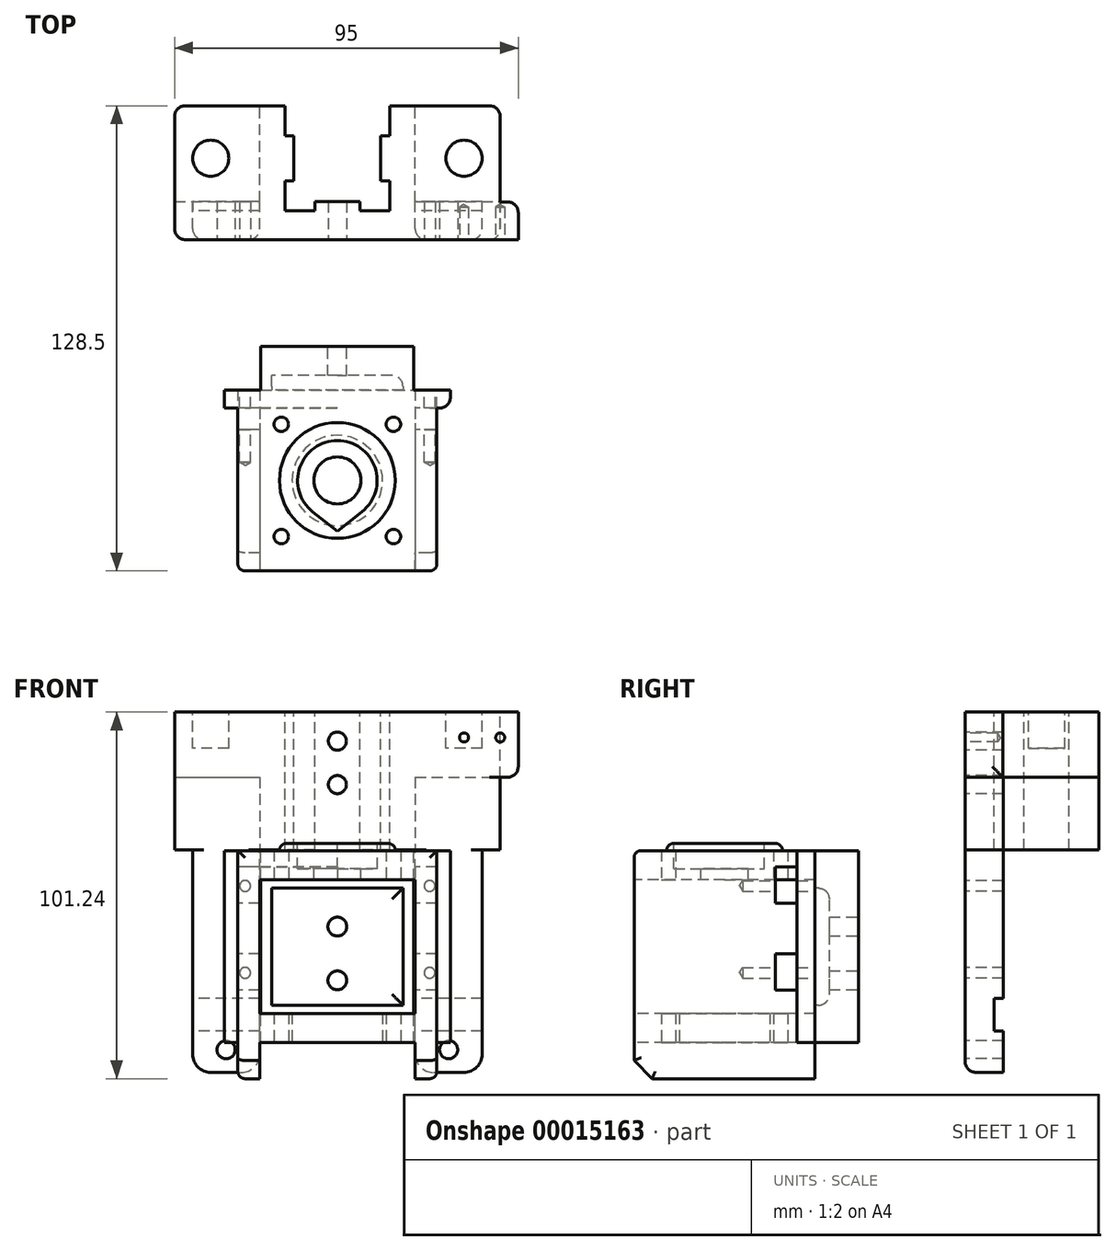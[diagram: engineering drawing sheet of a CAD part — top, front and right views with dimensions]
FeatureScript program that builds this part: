
annotation { "Feature Type Name" : "Feature", "Feature Type Description" : "" }
export const myFeature = defineFeature(function(context is Context, id is Id, definition is map)
    precondition{}
    {
        {
            var Q0;
            Q0=qCreatedBy(makeId("Top.planeOp"),FACE);
            var sketch = newSketch(context, id + "F0", { "sketchPlane" : qUnion([Q0])});
            skLineSegment(sketch, "E0.rect.bottom", {"start": v(-45, -18.5) * mm, "end": v(45, -18.5) * mm});
            skLineSegment(sketch, "E0.rect.top", {"start": v(-45, 18.5) * mm, "end": v(-14.5, 18.5) * mm});
            skLineSegment(sketch, "E0.rect.left", {"start": v(-45, -18.5) * mm, "end": v(-45, 18.5) * mm});
            skLineSegment(sketch, "E0.rect.right", {"start": v(45, -18.5) * mm, "end": v(45, 18.5) * mm});
            skPoint(sketch, "E0.rect.middle", {"position": v(0, 0) * mm});
            skPoint(sketch, "E1", {"position": v(0, 18.5) * mm});
            skLineSegment(sketch, "E2.rect.bottom", {"start": v(14.5, -10.5) * mm, "end": v(6.2, -10.5) * mm});
            skLineSegment(sketch, "E2.rect.left", {"start": v(14.5, -10.5) * mm, "end": v(14.5, -2.2) * mm});
            skLineSegment(sketch, "E2.rect.right", {"start": v(-14.5, -10.5) * mm, "end": v(-14.5, -2.2) * mm});
            skPoint(sketch, "E3.orphan", {"position": v(-14.5, 47.5) * mm});
            skPoint(sketch, "E4.orphan", {"position": v(14.5, 47.5) * mm});
            skLineSegment(sketch, "E5.trimOffspring", {"start": v(14.5, 18.5) * mm, "end": v(45, 18.5) * mm});
            skLineSegment(sketch, "E6", {"start": v(-6.2, -10.5) * mm, "end": v(-6.2, -8) * mm});
            skLineSegment(sketch, "E7", {"start": v(-6.2, -8) * mm, "end": v(6.2, -8) * mm});
            skLineSegment(sketch, "E8", {"start": v(6.2, -8) * mm, "end": v(6.2, -10.5) * mm});
            skLineSegment(sketch, "E9", {"start": v(14.5, 10.2) * mm, "end": v(12, 10.2) * mm});
            skLineSegment(sketch, "E10", {"start": v(12, 10.2) * mm, "end": v(12, -2.2) * mm});
            skLineSegment(sketch, "E11", {"start": v(12, -2.2) * mm, "end": v(14.5, -2.2) * mm});
            skLineSegment(sketch, "E12", {"start": v(-14.5, 10.2) * mm, "end": v(-12, 10.2) * mm});
            skLineSegment(sketch, "E13", {"start": v(-12, 10.2) * mm, "end": v(-12, -2.2) * mm});
            skLineSegment(sketch, "E14", {"start": v(-12, -2.2) * mm, "end": v(-14.5, -2.2) * mm});
            skLineSegment(sketch, "E15.trimOffspring", {"start": v(-14.5, 10.2) * mm, "end": v(-14.5, 18.5) * mm});
            skLineSegment(sketch, "E16.trimOffspring", {"start": v(14.5, 10.2) * mm, "end": v(14.5, 18.5) * mm});
            skLineSegment(sketch, "E17.trimOffspring", {"start": v(-6.2, -10.5) * mm, "end": v(-14.5, -10.5) * mm});
            skPoint(sketch, "E18", {"position": v(-12, 4) * mm});
            skPoint(sketch, "E19", {"position": v(12, 4) * mm});
            skCircle(sketch, "E20", {"center": v(35, 4) * mm, "radius": 5 * mm});
            skCircle(sketch, "E21", {"center": v(-35, 4) * mm, "radius": 5 * mm});
            skPoint(sketch, "E22", {"position": v(0, -8) * mm});
            skSolve(sketch);
        }
        {
            var Q0;
            Q0=makeQuery(id+"F0.imprint","IMPRINT",FACE,{"disambiguationData":[TD([[makeQuery(id+"F0.imprint","IMPRINT",EDGE,{"derivedFrom":sQuery(id+"F0.wireOp",EDGE,"E0.rect.bottom")}),1.0]])]});
            var Q1;
            Q1=makeQuery(id+"F0.imprint","IMPRINT",FACE,{"disambiguationData":[TD([[makeQuery(id+"F0.imprint","IMPRINT",EDGE,{"derivedFrom":sQuery(id+"F0.wireOp",EDGE,"E21")}),1.0]])]});
            var Q2;
            Q2=makeQuery(id+"F0.imprint","IMPRINT",FACE,{"disambiguationData":[TD([[makeQuery(id+"F0.imprint","IMPRINT",EDGE,{"derivedFrom":sQuery(id+"F0.wireOp",EDGE,"E20")}),1.0]])]});
            extrude(context, id + "F1", {"entities" : qUnion([Q0, Q1, Q2]), "oppositeDirection" : true, "depth" : 38 * mm});
        }
        {
            var Q0;
            Q0=makeQuery(id+"F0.imprint","IMPRINT",FACE,{"disambiguationData":[TD([[makeQuery(id+"F0.imprint","IMPRINT",EDGE,{"derivedFrom":sQuery(id+"F0.wireOp",EDGE,"E21")}),1.0]])]});
            var Q1;
            Q1=makeQuery(id+"F0.imprint","IMPRINT",FACE,{"disambiguationData":[TD([[makeQuery(id+"F0.imprint","IMPRINT",EDGE,{"derivedFrom":sQuery(id+"F0.wireOp",EDGE,"E20")}),1.0]])]});
            extrude(context, id + "F2", {"entities" : qUnion([Q0, Q1]), "operationType" : NewBodyOperationType.REMOVE, "oppositeDirection" : true, "depth" : 10 * mm});
        }
        {
            var Q0;
            Q0=makeQuery(id+"F1.opExtrude","CAP_FACE",FACE,{"disambiguationData":[OSD([sQuery(id+"F0.wireOp",EDGE,"E0.rect.bottom"),sQuery(id+"F0.wireOp",EDGE,"E0.rect.top"),sQuery(id+"F0.wireOp",EDGE,"E0.rect.left"),sQuery(id+"F0.wireOp",EDGE,"E0.rect.right"),sQuery(id+"F0.wireOp",EDGE,"E2.rect.bottom"),sQuery(id+"F0.wireOp",EDGE,"E2.rect.left"),sQuery(id+"F0.wireOp",EDGE,"E2.rect.right"),sQuery(id+"F0.wireOp",EDGE,"E5.trimOffspring"),sQuery(id+"F0.wireOp",EDGE,"E6"),sQuery(id+"F0.wireOp",EDGE,"E7"),sQuery(id+"F0.wireOp",EDGE,"E8"),sQuery(id+"F0.wireOp",EDGE,"E9"),sQuery(id+"F0.wireOp",EDGE,"E10"),sQuery(id+"F0.wireOp",EDGE,"E11"),sQuery(id+"F0.wireOp",EDGE,"E12"),sQuery(id+"F0.wireOp",EDGE,"E13"),sQuery(id+"F0.wireOp",EDGE,"E14"),sQuery(id+"F0.wireOp",EDGE,"E15.trimOffspring"),sQuery(id+"F0.wireOp",EDGE,"E16.trimOffspring"),sQuery(id+"F0.wireOp",EDGE,"E17.trimOffspring")])],"isStart":false});
            var sketch = newSketch(context, id + "F3", { "sketchPlane" : qUnion([Q0])});
            skLineSegment(sketch, "E23.0", {"start": v(-6.2, 10.5) * mm, "end": v(-14.5, 10.5) * mm});
            skPoint(sketch, "E23.1", {"position": v(-14.5, 10.5) * mm});
            skLineSegment(sketch, "E23.2", {"start": v(14.5, 10.5) * mm, "end": v(6.2, 10.5) * mm});
            skLineSegment(sketch, "E23.3", {"start": v(-45, 18.5) * mm, "end": v(45, 18.5) * mm});
            skLineSegment(sketch, "E23.4", {"start": v(14.5, 10.5) * mm, "end": v(14.5, 2.2) * mm});
            skLineSegment(sketch, "E23.5", {"start": v(12, 2.2) * mm, "end": v(14.5, 2.2) * mm});
            skLineSegment(sketch, "E23.6", {"start": v(12, -10.2) * mm, "end": v(12, 2.2) * mm});
            skLineSegment(sketch, "E23.7", {"start": v(14.5, -10.2) * mm, "end": v(12, -10.2) * mm});
            skLineSegment(sketch, "E23.8", {"start": v(14.5, -10.2) * mm, "end": v(14.5, -18.5) * mm});
            skLineSegment(sketch, "E23.9", {"start": v(6.2, 8) * mm, "end": v(6.2, 10.5) * mm});
            skLineSegment(sketch, "E23.10", {"start": v(-6.2, 8) * mm, "end": v(6.2, 8) * mm});
            skLineSegment(sketch, "E23.11", {"start": v(-6.2, 10.5) * mm, "end": v(-6.2, 8) * mm});
            skLineSegment(sketch, "E23.12", {"start": v(-14.5, 10.5) * mm, "end": v(-14.5, 2.2) * mm});
            skLineSegment(sketch, "E23.13", {"start": v(-12, 2.2) * mm, "end": v(-14.5, 2.2) * mm});
            skLineSegment(sketch, "E23.14", {"start": v(-12, -10.2) * mm, "end": v(-12, 2.2) * mm});
            skLineSegment(sketch, "E23.15", {"start": v(-14.5, -10.2) * mm, "end": v(-12, -10.2) * mm});
            skLineSegment(sketch, "E23.16", {"start": v(-14.5, -10.2) * mm, "end": v(-14.5, -18.5) * mm});
            skLineSegment(sketch, "E23.17", {"start": v(45, 18.5) * mm, "end": v(45, -18.5) * mm});
            skLineSegment(sketch, "E23.18", {"start": v(14.5, -18.5) * mm, "end": v(45, -18.5) * mm});
            skLineSegment(sketch, "E23.19", {"start": v(-45, -18.5) * mm, "end": v(-14.5, -18.5) * mm});
            skLineSegment(sketch, "E23.20", {"start": v(-45, 18.5) * mm, "end": v(-45, -18.5) * mm});
            skPoint(sketch, "E24", {"position": v(0, 18.5) * mm});
            skLineSegment(sketch, "E25", {"start": v(-21.5, 18.5) * mm, "end": v(-21.5, -18.5) * mm});
            skLineSegment(sketch, "E26", {"start": v(21.5, 18.5) * mm, "end": v(21.5, -18.5) * mm});
            skLineSegment(sketch, "E27", {"start": v(-45, 8) * mm, "end": v(-21.5, 8) * mm});
            skLineSegment(sketch, "E28", {"start": v(21.5, 8) * mm, "end": v(45, 8) * mm});
            skLineSegment(sketch, "E29", {"start": v(40, 18.5) * mm, "end": v(40, 8) * mm});
            skLineSegment(sketch, "E30", {"start": v(-40, 18.5) * mm, "end": v(-40, 8) * mm});
            skSolve(sketch);
        }
        {
            var Q0;
            {var subQ4=sQuery(id+"F3.wireOp",EDGE,"E23.19");var subQ6=sQuery(id+"F3.wireOp",EDGE,"E23.20");var subQ8=makeQuery(id+"F3.imprint","INTERSECT",VERTEX,{"derivedFrom":[subQ4,subQ6]});Q0=makeQuery(id+"F3.imprint","IMPRINT",FACE,{"disambiguationData":[TD([[makeQuery(id+"F3.imprint","IMPRINT",EDGE,{"disambiguationData":[TD([[subQ8,-1.0]])],"derivedFrom":subQ4}),1.0]])]});}
            var Q1;
            {var subQ4=sQuery(id+"F3.wireOp",EDGE,"E23.17");var subQ6=sQuery(id+"F3.wireOp",EDGE,"E23.18");var subQ8=makeQuery(id+"F3.imprint","INTERSECT",VERTEX,{"derivedFrom":[subQ4,subQ6]});Q1=makeQuery(id+"F3.imprint","IMPRINT",FACE,{"disambiguationData":[TD([[makeQuery(id+"F3.imprint","IMPRINT",EDGE,{"disambiguationData":[TD([[subQ8,1.0]])],"derivedFrom":subQ4}),-1.0]])]});}
            extrude(context, id + "F4", {"entities" : qUnion([Q0, Q1]), "operationType" : NewBodyOperationType.REMOVE, "oppositeDirection" : true, "depth" : 20 * mm});
        }
        {
            var Q0;
            {var subQ0=sQuery(id+"F3.wireOp",EDGE,"E30");Q0=makeQuery(id+"F3.imprint","IMPRINT",FACE,{"disambiguationData":[TD([[makeQuery(id+"F3.imprint","IMPRINT",EDGE,{"derivedFrom":subQ0}),1.0]])]});}
            var Q1;
            {var subQ0=sQuery(id+"F3.wireOp",EDGE,"E29");Q1=makeQuery(id+"F3.imprint","IMPRINT",FACE,{"disambiguationData":[TD([[makeQuery(id+"F3.imprint","IMPRINT",EDGE,{"derivedFrom":subQ0}),-1.0]])]});}
            extrude(context, id + "F5", {"entities" : qUnion([Q0, Q1]), "operationType" : NewBodyOperationType.ADD, "depth" : 61.5 * mm});
        }
        {
            var Q0;
            Q0=makeQuery(id+"F5.opExtrude","SWEPT_FACE",FACE,{"disambiguationData":[OSD([sQuery(id+"F3.wireOp",EDGE,"E30")])]});
            var sketch = newSketch(context, id + "F6", { "sketchPlane" : qUnion([Q0])});
            skLineSegment(sketch, "E31.0", {"start": v(18.5, -38) * mm, "end": v(-18.5, -38) * mm});
            skLineSegment(sketch, "E32.bottom", {"start": v(8, -79.1) * mm, "end": v(10.5, -79.1) * mm});
            skLineSegment(sketch, "E32.top", {"start": v(8, -88.1) * mm, "end": v(10.5, -88.1) * mm});
            skLineSegment(sketch, "E32.left", {"start": v(8, -79.1) * mm, "end": v(8, -88.1) * mm});
            skLineSegment(sketch, "E32.right", {"start": v(10.5, -79.1) * mm, "end": v(10.5, -88.1) * mm});
            skSolve(sketch);
        }
        {
            var Q0;
            Q0=makeQuery(id+"F6.imprint","IMPRINT",FACE,{"disambiguationData":[TD([[makeQuery(id+"F6.imprint","IMPRINT",EDGE,{"derivedFrom":sQuery(id+"F6.wireOp",EDGE,"E32.bottom")}),-1.0]])]});
            extrude(context, id + "F7", {"entities" : qUnion([Q0]), "operationType" : NewBodyOperationType.REMOVE, "endBound" : BoundingType.THROUGH_ALL, "oppositeDirection" : true, "depth" : 25 * mm});
        }
        {
            var Q0;
            {var subQ0=sQuery(id+"F3.wireOp",EDGE,"E23.3");Q0=makeQuery(id+"F5.boolean.opBoolean","MERGE",FACE,{"derivedFrom":[makeQuery(id+"F1.opExtrude","SWEPT_FACE",FACE,{"disambiguationData":[OSD([sQuery(id+"F0.wireOp",EDGE,"E0.rect.bottom")])]}),makeQuery(id+"F5.opExtrude","SWEPT_FACE",FACE,{"disambiguationData":[OSD([subQ0]),TDD([makeQuery(id+"F3.imprint","IMPRINT",EDGE,{"disambiguationData":[TD([[makeQuery(id+"F3.imprint","INTERSECT",VERTEX,{"derivedFrom":[subQ0,sQuery(id+"F3.wireOp",EDGE,"E25")]}),1.0]])],"derivedFrom":subQ0})])]}),makeQuery(id+"F5.opExtrude","SWEPT_FACE",FACE,{"disambiguationData":[OSD([subQ0]),TDD([makeQuery(id+"F3.imprint","IMPRINT",EDGE,{"disambiguationData":[TD([[makeQuery(id+"F3.imprint","INTERSECT",VERTEX,{"derivedFrom":[subQ0,sQuery(id+"F3.wireOp",EDGE,"E26")]}),-1.0]])],"derivedFrom":subQ0})])]})]});}
            var sketch = newSketch(context, id + "F8", { "sketchPlane" : qUnion([Q0])});
            skPoint(sketch, "E33.0", {"position": v(0, 0) * mm});
            skLineSegment(sketch, "E34.bottom", {"start": v(30, 0) * mm, "end": v(50, 0) * mm});
            skLineSegment(sketch, "E34.right", {"start": v(50, 0) * mm, "end": v(50, -10) * mm});
            skPoint(sketch, "E35", {"position": v(35, -7) * mm});
            skPoint(sketch, "E36", {"position": v(45, -7) * mm});
            skPoint(sketch, "E37", {"position": v(0, -8) * mm});
            skPoint(sketch, "E38", {"position": v(0, -20) * mm});
            skPoint(sketch, "E39", {"position": v(-30.75, -93.25) * mm});
            skPoint(sketch, "E40", {"position": v(30.75, -93.25) * mm});
            skLineSegment(sketch, "E41.0", {"start": v(45, -38) * mm, "end": v(45, -18) * mm});
            skLineSegment(sketch, "E42.0", {"start": v(21.5, -18) * mm, "end": v(45, -18) * mm});
            skPoint(sketch, "E43", {"position": v(-25.5, -48) * mm});
            skPoint(sketch, "E44", {"position": v(-25.5, -72) * mm});
            skPoint(sketch, "E45", {"position": v(25.5, -48) * mm});
            skPoint(sketch, "E46", {"position": v(25.5, -72) * mm});
            skLineSegment(sketch, "E47.0", {"start": v(-40, -99.5) * mm, "end": v(-40, -38) * mm});
            skLineSegment(sketch, "E47.1", {"start": v(40, -99.5) * mm, "end": v(40, -38) * mm});
            skLineSegment(sketch, "E48", {"start": v(-25.5, -48) * mm, "end": v(-40, -48) * mm});
            skLineSegment(sketch, "E49", {"start": v(25.5, -48) * mm, "end": v(40, -48) * mm});
            skLineSegment(sketch, "E50", {"start": v(-25.5, -72) * mm, "end": v(-40, -72) * mm});
            skLineSegment(sketch, "E51", {"start": v(25.5, -72) * mm, "end": v(40, -72) * mm});
            skLineSegment(sketch, "E52.0", {"start": v(40, -88.1) * mm, "end": v(21.5, -88.1) * mm});
            skLineSegment(sketch, "E52.1", {"start": v(-21.5, -88.1) * mm, "end": v(-40, -88.1) * mm});
            skPoint(sketch, "E53", {"position": v(-30.75, -99.5) * mm});
            skLineSegment(sketch, "E54", {"start": v(-30.75, -93.25) * mm, "end": v(-21.5, -93.25) * mm});
            skLineSegment(sketch, "E55", {"start": v(-30.75, -93.25) * mm, "end": v(-40, -93.25) * mm});
            skLineSegment(sketch, "E56", {"start": v(30.75, -93.25) * mm, "end": v(40, -93.25) * mm});
            skLineSegment(sketch, "E57", {"start": v(30.75, -93.25) * mm, "end": v(21.5, -93.25) * mm});
            skLineSegment(sketch, "E58", {"start": v(50, -10) * mm, "end": v(50, -18) * mm});
            skLineSegment(sketch, "E59", {"start": v(50, -18) * mm, "end": v(45, -18) * mm});
            skPoint(sketch, "E60.trimOffspring.end.orphan", {"position": v(45, 0) * mm});
            skSolve(sketch);
        }
        {
            var Q0;
            {var subQ4=sQuery(id+"F8.wireOp",EDGE,"E34.right");Q0=makeQuery(id+"F8.imprint","IMPRINT",FACE,{"disambiguationData":[TD([[makeQuery(id+"F8.imprint","IMPRINT",EDGE,{"derivedFrom":subQ4}),-1.0]])]});}
            extrude(context, id + "F9", {"entities" : qUnion([Q0]), "operationType" : NewBodyOperationType.ADD, "oppositeDirection" : true, "depth" : 10.45 * mm});
        }
        {
            var Q0;
            Q0=sQuery(id+"F8.wireOp",VERTEX,"E36");
            var Q1;
            Q1=sQuery(id+"F8.wireOp",VERTEX,"E35");
            var Q2;
            Q2=makeQuery(id+"F1.opExtrude","SWEPT_BODY",BODY,{"disambiguationData":[OSD([sQuery(id+"F0.wireOp",EDGE,"E0.rect.bottom"),sQuery(id+"F0.wireOp",EDGE,"E0.rect.top"),sQuery(id+"F0.wireOp",EDGE,"E0.rect.left"),sQuery(id+"F0.wireOp",EDGE,"E0.rect.right"),sQuery(id+"F0.wireOp",EDGE,"E2.rect.bottom"),sQuery(id+"F0.wireOp",EDGE,"E2.rect.left"),sQuery(id+"F0.wireOp",EDGE,"E2.rect.right"),sQuery(id+"F0.wireOp",EDGE,"E5.trimOffspring"),sQuery(id+"F0.wireOp",EDGE,"E6"),sQuery(id+"F0.wireOp",EDGE,"E7"),sQuery(id+"F0.wireOp",EDGE,"E8"),sQuery(id+"F0.wireOp",EDGE,"E9"),sQuery(id+"F0.wireOp",EDGE,"E10"),sQuery(id+"F0.wireOp",EDGE,"E11"),sQuery(id+"F0.wireOp",EDGE,"E12"),sQuery(id+"F0.wireOp",EDGE,"E13"),sQuery(id+"F0.wireOp",EDGE,"E14"),sQuery(id+"F0.wireOp",EDGE,"E15.trimOffspring"),sQuery(id+"F0.wireOp",EDGE,"E16.trimOffspring"),sQuery(id+"F0.wireOp",EDGE,"E17.trimOffspring")])]});
            hole(context, id + "F10", {"style" : HoleStyle.SIMPLE, "holeDiameter" : 2.5 * mm, "endStyle" : HoleEndStyle.BLIND, "holeDepth" : 9 * mm, "locations" : qUnion([Q0, Q1]), "scope" : qUnion([Q2])});
        }
        {
            var Q0;
            Q0=sQuery(id+"F8.wireOp",VERTEX,"E38");
            var Q1;
            Q1=sQuery(id+"F8.wireOp",VERTEX,"E37");
            var Q2;
            Q2=makeQuery(id+"F1.opExtrude","SWEPT_BODY",BODY,{"disambiguationData":[OSD([sQuery(id+"F0.wireOp",EDGE,"E0.rect.bottom"),sQuery(id+"F0.wireOp",EDGE,"E0.rect.top"),sQuery(id+"F0.wireOp",EDGE,"E0.rect.left"),sQuery(id+"F0.wireOp",EDGE,"E0.rect.right"),sQuery(id+"F0.wireOp",EDGE,"E2.rect.bottom"),sQuery(id+"F0.wireOp",EDGE,"E2.rect.left"),sQuery(id+"F0.wireOp",EDGE,"E2.rect.right"),sQuery(id+"F0.wireOp",EDGE,"E5.trimOffspring"),sQuery(id+"F0.wireOp",EDGE,"E6"),sQuery(id+"F0.wireOp",EDGE,"E7"),sQuery(id+"F0.wireOp",EDGE,"E8"),sQuery(id+"F0.wireOp",EDGE,"E9"),sQuery(id+"F0.wireOp",EDGE,"E10"),sQuery(id+"F0.wireOp",EDGE,"E11"),sQuery(id+"F0.wireOp",EDGE,"E12"),sQuery(id+"F0.wireOp",EDGE,"E13"),sQuery(id+"F0.wireOp",EDGE,"E14"),sQuery(id+"F0.wireOp",EDGE,"E15.trimOffspring"),sQuery(id+"F0.wireOp",EDGE,"E16.trimOffspring"),sQuery(id+"F0.wireOp",EDGE,"E17.trimOffspring")])]});
            hole(context, id + "F11", {"style" : HoleStyle.SIMPLE, "holeDiameter" : 5 * mm, "endStyle" : HoleEndStyle.THROUGH, "locations" : qUnion([Q0, Q1]), "scope" : qUnion([Q2])});
        }
        {
            var Q0;
            Q0=sQuery(id+"F8.wireOp",VERTEX,"E40");
            var Q1;
            Q1=sQuery(id+"F8.wireOp",VERTEX,"E39");
            var Q2;
            Q2=makeQuery(id+"F1.opExtrude","SWEPT_BODY",BODY,{"disambiguationData":[OSD([sQuery(id+"F0.wireOp",EDGE,"E0.rect.bottom"),sQuery(id+"F0.wireOp",EDGE,"E0.rect.top"),sQuery(id+"F0.wireOp",EDGE,"E0.rect.left"),sQuery(id+"F0.wireOp",EDGE,"E0.rect.right"),sQuery(id+"F0.wireOp",EDGE,"E2.rect.bottom"),sQuery(id+"F0.wireOp",EDGE,"E2.rect.left"),sQuery(id+"F0.wireOp",EDGE,"E2.rect.right"),sQuery(id+"F0.wireOp",EDGE,"E5.trimOffspring"),sQuery(id+"F0.wireOp",EDGE,"E6"),sQuery(id+"F0.wireOp",EDGE,"E7"),sQuery(id+"F0.wireOp",EDGE,"E8"),sQuery(id+"F0.wireOp",EDGE,"E9"),sQuery(id+"F0.wireOp",EDGE,"E10"),sQuery(id+"F0.wireOp",EDGE,"E11"),sQuery(id+"F0.wireOp",EDGE,"E12"),sQuery(id+"F0.wireOp",EDGE,"E13"),sQuery(id+"F0.wireOp",EDGE,"E14"),sQuery(id+"F0.wireOp",EDGE,"E15.trimOffspring"),sQuery(id+"F0.wireOp",EDGE,"E16.trimOffspring"),sQuery(id+"F0.wireOp",EDGE,"E17.trimOffspring")])]});
            hole(context, id + "F12", {"style" : HoleStyle.SIMPLE, "holeDiameter" : 5 * mm, "endStyle" : HoleEndStyle.THROUGH, "locations" : qUnion([Q0, Q1]), "scope" : qUnion([Q2])});
        }
        {
            var Q0;
            Q0=sQuery(id+"F8.wireOp",VERTEX,"E44");
            var Q1;
            Q1=sQuery(id+"F8.wireOp",VERTEX,"E43");
            var Q2;
            Q2=sQuery(id+"F8.wireOp",VERTEX,"E49.start");
            var Q3;
            Q3=sQuery(id+"F8.wireOp",VERTEX,"E46");
            var Q4;
            Q4=makeQuery(id+"F1.opExtrude","SWEPT_BODY",BODY,{"disambiguationData":[OSD([sQuery(id+"F0.wireOp",EDGE,"E0.rect.bottom"),sQuery(id+"F0.wireOp",EDGE,"E0.rect.top"),sQuery(id+"F0.wireOp",EDGE,"E0.rect.left"),sQuery(id+"F0.wireOp",EDGE,"E0.rect.right"),sQuery(id+"F0.wireOp",EDGE,"E2.rect.bottom"),sQuery(id+"F0.wireOp",EDGE,"E2.rect.left"),sQuery(id+"F0.wireOp",EDGE,"E2.rect.right"),sQuery(id+"F0.wireOp",EDGE,"E5.trimOffspring"),sQuery(id+"F0.wireOp",EDGE,"E6"),sQuery(id+"F0.wireOp",EDGE,"E7"),sQuery(id+"F0.wireOp",EDGE,"E8"),sQuery(id+"F0.wireOp",EDGE,"E9"),sQuery(id+"F0.wireOp",EDGE,"E10"),sQuery(id+"F0.wireOp",EDGE,"E11"),sQuery(id+"F0.wireOp",EDGE,"E12"),sQuery(id+"F0.wireOp",EDGE,"E13"),sQuery(id+"F0.wireOp",EDGE,"E14"),sQuery(id+"F0.wireOp",EDGE,"E15.trimOffspring"),sQuery(id+"F0.wireOp",EDGE,"E16.trimOffspring"),sQuery(id+"F0.wireOp",EDGE,"E17.trimOffspring")])]});
            hole(context, id + "F13", {"style" : HoleStyle.SIMPLE, "holeDiameter" : 3 * mm, "endStyle" : HoleEndStyle.THROUGH, "locations" : qUnion([Q0, Q1, Q2, Q3]), "scope" : qUnion([Q4])});
        }
        {
            var Q0;
            Q0=makeQuery(id+"F5.opExtrude","CAP_EDGE",EDGE,{"disambiguationData":[OSD([sQuery(id+"F3.wireOp",EDGE,"E30")])],"isStart":false});
            var Q1;
            Q1=makeQuery(id+"F5.opExtrude","CAP_EDGE",EDGE,{"disambiguationData":[OSD([sQuery(id+"F3.wireOp",EDGE,"E25")])],"isStart":false});
            var Q2;
            Q2=makeQuery(id+"F5.opExtrude","CAP_EDGE",EDGE,{"disambiguationData":[OSD([sQuery(id+"F3.wireOp",EDGE,"E26")])],"isStart":false});
            var Q3;
            Q3=makeQuery(id+"F5.opExtrude","CAP_EDGE",EDGE,{"disambiguationData":[OSD([sQuery(id+"F3.wireOp",EDGE,"E29")])],"isStart":false});
            fillet(context, id + "F14", {"entities" : qUnion([Q0, Q1, Q2, Q3]), "radius" : 5 * mm, "tangentPropagation" : true, "allowEdgeOverflow" : false});
        }
        {
            var Q0;
            Q0=makeQuery(id+"F5.opExtrude","SWEPT_EDGE",EDGE,{"disambiguationData":[OSD([sQuery(id+"F3.wireOp",EDGE,"E23.3"),sQuery(id+"F3.wireOp",EDGE,"E30")])]});
            var Q1;
            Q1=makeQuery(id+"F5.opExtrude","SWEPT_EDGE",EDGE,{"disambiguationData":[OSD([sQuery(id+"F3.wireOp",EDGE,"E23.3"),sQuery(id+"F3.wireOp",EDGE,"E26")])]});
            var Q2;
            Q2=makeQuery(id+"F1.opExtrude","SWEPT_EDGE",EDGE,{"disambiguationData":[OSD([sQuery(id+"F0.wireOp",EDGE,"E0.rect.bottom"),sQuery(id+"F0.wireOp",EDGE,"E0.rect.left")])]});
            var Q3;
            Q3=makeQuery(id+"F1.opExtrude","SWEPT_EDGE",EDGE,{"disambiguationData":[OSD([sQuery(id+"F0.wireOp",EDGE,"E0.rect.bottom"),sQuery(id+"F0.wireOp",EDGE,"E0.rect.right")])]});
            var Q4;
            Q4=makeQuery(id+"F1.opExtrude","SWEPT_EDGE",EDGE,{"disambiguationData":[OSD([sQuery(id+"F0.wireOp",EDGE,"E0.rect.top"),sQuery(id+"F0.wireOp",EDGE,"E0.rect.left")])]});
            var Q5;
            Q5=makeQuery(id+"F1.opExtrude","SWEPT_EDGE",EDGE,{"disambiguationData":[OSD([sQuery(id+"F0.wireOp",EDGE,"E0.rect.right"),sQuery(id+"F0.wireOp",EDGE,"E5.trimOffspring")])]});
            var Q6;
            Q6=makeQuery(id+"F9.opExtrude","CAP_EDGE",EDGE,{"disambiguationData":[OSD([sQuery(id+"F8.wireOp",EDGE,"E34.right"),sQuery(id+"F8.wireOp",EDGE,"E58")])],"isStart":false});
            var Q7;
            Q7=makeQuery(id+"F9.opExtrude","SWEPT_EDGE",EDGE,{"disambiguationData":[OSD([sQuery(id+"F8.wireOp",EDGE,"E58"),sQuery(id+"F8.wireOp",EDGE,"E59")])]});
            var Q8;
            Q8=makeQuery(id+"F4.boolean.opBoolean","COPY",EDGE,{"derivedFrom":makeQuery(id+"F4.opExtrude","SWEPT_EDGE",EDGE,{"disambiguationData":[OSD([sQuery(id+"F3.wireOp",EDGE,"E23.17"),sQuery(id+"F3.wireOp",EDGE,"E28")])]})});
            var Q9;
            Q9=makeQuery(id+"F4.boolean.opBoolean","COPY",EDGE,{"derivedFrom":makeQuery(id+"F4.opExtrude","SWEPT_EDGE",EDGE,{"disambiguationData":[OSD([sQuery(id+"F3.wireOp",EDGE,"E23.20"),sQuery(id+"F3.wireOp",EDGE,"E27")])]})});
            fillet(context, id + "F15", {"entities" : qUnion([Q0, Q1, Q2, Q3, Q4, Q5, Q6, Q7, Q8, Q9]), "radius" : 3 * mm, "tangentPropagation" : true, "allowEdgeOverflow" : false});
        }
        {
            var Q0;
            Q0=qCreatedBy(makeId("Front.planeOp"),FACE);
            var sketch = newSketch(context, id + "F16", { "sketchPlane" : qUnion([Q0])});
            skLineSegment(sketch, "E61.0", {"start": v(-21.25, -38.24) * mm, "end": v(21.25, -38.24) * mm});
            skLineSegment(sketch, "E62.0", {"start": v(21.25, -91.24) * mm, "end": v(21.25, -38.24) * mm});
            skLineSegment(sketch, "E63.0", {"start": v(-21.25, -91.24) * mm, "end": v(-21.25, -38.24) * mm});
            skPoint(sketch, "E64", {"position": v(0, -38.24) * mm});
            skLineSegment(sketch, "E65", {"start": v(-21.25, -91.24) * mm, "end": v(21.25, -91.24) * mm});
            skLineSegment(sketch, "E66", {"start": v(0, -38.24) * mm, "end": v(0, -91.24) * mm});
            skPoint(sketch, "E67", {"position": v(0, -53.97) * mm});
            skPoint(sketch, "E68", {"position": v(0, -64.74) * mm});
            skSolve(sketch);
        }
        {
            var Q0;
            {var subQ2=sQuery(id+"F16.wireOp",EDGE,"E63.0");Q0=makeQuery(id+"F16.imprint","IMPRINT",FACE,{"disambiguationData":[TD([[makeQuery(id+"F16.imprint","IMPRINT",EDGE,{"derivedFrom":subQ2}),-1.0]])]});}
            var Q1;
            {var subQ2=sQuery(id+"F16.wireOp",EDGE,"E62.0");Q1=makeQuery(id+"F16.imprint","IMPRINT",FACE,{"disambiguationData":[TD([[makeQuery(id+"F16.imprint","IMPRINT",EDGE,{"derivedFrom":subQ2}),1.0]])]});}
            extrude(context, id + "F17", {"entities" : qUnion([Q0, Q1]), "depth" : 10 * mm});
        }
        {
            var Q0;
            Q0=makeQuery(id+"F17.opExtrude","SWEPT_BODY",BODY,{"disambiguationData":[OSD([sQuery(id+"F16.wireOp",EDGE,"E61.0"),sQuery(id+"F16.wireOp",EDGE,"E62.0"),sQuery(id+"F16.wireOp",EDGE,"E63.0"),sQuery(id+"F16.wireOp",EDGE,"E65")])]});
            transform(context, id + "F18", {"entities" : qUnion([Q0]), "transformType" : TransformType.TRANSLATION_3D, "dx" : 0 * mm, "dy" : -50 * mm, "dz" : 0 * mm, "makeCopy" : false});
        }
        {
            var Q0;
            Q0=makeQuery(id+"F17.opExtrude","CAP_FACE",FACE,{"disambiguationData":[OSD([sQuery(id+"F16.wireOp",EDGE,"E61.0"),sQuery(id+"F16.wireOp",EDGE,"E62.0"),sQuery(id+"F16.wireOp",EDGE,"E63.0"),sQuery(id+"F16.wireOp",EDGE,"E65")])],"isStart":false});
            var sketch = newSketch(context, id + "F19", { "sketchPlane" : qUnion([Q0])});
            skLineSegment(sketch, "E69", {"start": v(-31.25, -38.24) * mm, "end": v(-31.25, -91.24) * mm});
            skLineSegment(sketch, "E70", {"start": v(31.25, -38.24) * mm, "end": v(31.25, -91.24) * mm});
            skLineSegment(sketch, "E71", {"start": v(-21.25, -46.24) * mm, "end": v(21.25, -46.24) * mm});
            skLineSegment(sketch, "E72", {"start": v(21.25, -46.24) * mm, "end": v(21.25, -83.24) * mm});
            skLineSegment(sketch, "E73", {"start": v(21.25, -83.24) * mm, "end": v(-21.25, -83.24) * mm});
            skLineSegment(sketch, "E74", {"start": v(-21.25, -83.24) * mm, "end": v(-21.25, -46.24) * mm});
            skLineSegment(sketch, "E75", {"start": v(-31.25, -38.24) * mm, "end": v(31.25, -38.24) * mm});
            skLineSegment(sketch, "E76", {"start": v(31.25, -91.24) * mm, "end": v(-31.25, -91.24) * mm});
            skSolve(sketch);
        }
        {
            var Q0;
            {var subQ4=sQuery(id+"F19.wireOp",EDGE,"E69");Q0=makeQuery(id+"F19.imprint","IMPRINT",FACE,{"disambiguationData":[TD([[makeQuery(id+"F19.imprint","IMPRINT",EDGE,{"derivedFrom":subQ4}),1.0]])]});}
            var Q1;
            {var subQ1=sQuery(id+"F19.wireOp",EDGE,"E71");Q1=makeQuery(id+"F19.imprint","IMPRINT",FACE,{"disambiguationData":[TD([[makeQuery(id+"F19.imprint","IMPRINT",EDGE,{"derivedFrom":subQ1}),1.0]])]});}
            var Q2;
            {var subQ6=sQuery(id+"F19.wireOp",EDGE,"E70");Q2=makeQuery(id+"F19.imprint","IMPRINT",FACE,{"disambiguationData":[TD([[makeQuery(id+"F19.imprint","IMPRINT",EDGE,{"derivedFrom":subQ6}),-1.0]])]});}
            var Q3;
            {var subQ1=sQuery(id+"F19.wireOp",EDGE,"E73");Q3=makeQuery(id+"F19.imprint","IMPRINT",FACE,{"disambiguationData":[TD([[makeQuery(id+"F19.imprint","IMPRINT",EDGE,{"derivedFrom":subQ1}),1.0]])]});}
            var Q4;
            Q4=makeQuery(id+"F19.imprint","IMPRINT",FACE,{"disambiguationData":[TD([[makeQuery(id+"F19.imprint","IMPRINT",EDGE,{"derivedFrom":sQuery(id+"F19.wireOp",EDGE,"E71")}),-1.0]])]});
            extrude(context, id + "F20", {"entities" : qUnion([Q0, Q1, Q2, Q3, Q4]), "operationType" : NewBodyOperationType.ADD, "depth" : 50 * mm});
        }
        {
            var Q0;
            Q0=makeQuery(id+"F20.opExtrude","CAP_FACE",FACE,{"disambiguationData":[OSD([sQuery(id+"F19.wireOp",EDGE,"E69"),sQuery(id+"F19.wireOp",EDGE,"E70"),sQuery(id+"F19.wireOp",EDGE,"E75"),sQuery(id+"F19.wireOp",EDGE,"E76")])],"isStart":false});
            var sketch = newSketch(context, id + "F21", { "sketchPlane" : qUnion([Q0])});
            skLineSegment(sketch, "E77.bottom", {"start": v(-21.5, -46.24) * mm, "end": v(21.5, -46.24) * mm});
            skLineSegment(sketch, "E77.top", {"start": v(-21.5, -83.24) * mm, "end": v(21.5, -83.24) * mm});
            skLineSegment(sketch, "E77.left", {"start": v(-21.5, -46.24) * mm, "end": v(-21.5, -83.24) * mm});
            skLineSegment(sketch, "E77.right", {"start": v(21.5, -46.24) * mm, "end": v(21.5, -83.24) * mm});
            skPoint(sketch, "E78", {"position": v(0, -38.24) * mm});
            skLineSegment(sketch, "E79", {"start": v(0, -38.24) * mm, "end": v(0, -91.24) * mm});
            skLineSegment(sketch, "E80", {"start": v(0, -46.24) * mm, "end": v(0, -83.24) * mm});
            skSolve(sketch);
        }
        {
            var Q0;
            {var subQ1=sQuery(id+"F21.wireOp",EDGE,"E77.left");Q0=makeQuery(id+"F21.imprint","IMPRINT",FACE,{"disambiguationData":[TD([[makeQuery(id+"F21.imprint","IMPRINT",EDGE,{"derivedFrom":subQ1}),1.0]])]});}
            var Q1;
            {var subQ1=sQuery(id+"F21.wireOp",EDGE,"E77.right");Q1=makeQuery(id+"F21.imprint","IMPRINT",FACE,{"disambiguationData":[TD([[makeQuery(id+"F21.imprint","IMPRINT",EDGE,{"derivedFrom":subQ1}),-1.0]])]});}
            extrude(context, id + "F22", {"entities" : qUnion([Q0, Q1]), "operationType" : NewBodyOperationType.REMOVE, "oppositeDirection" : true, "depth" : 50 * mm});
        }
        {
            var Q0;
            Q0=makeQuery(id+"F20.opExtrude","CAP_FACE",FACE,{"disambiguationData":[OSD([sQuery(id+"F19.wireOp",EDGE,"E69"),sQuery(id+"F19.wireOp",EDGE,"E70"),sQuery(id+"F19.wireOp",EDGE,"E75"),sQuery(id+"F19.wireOp",EDGE,"E76")])],"isStart":false});
            var sketch = newSketch(context, id + "F23", { "sketchPlane" : qUnion([Q0])});
            skLineSegment(sketch, "E81", {"start": v(-27.5, -38.24) * mm, "end": v(-27.5, -91.24) * mm});
            skLineSegment(sketch, "E82", {"start": v(27.5, -38.24) * mm, "end": v(27.5, -91.24) * mm});
            skSolve(sketch);
        }
        {
            var Q0;
            {var subQ1=sQuery(id+"F23.wireOp",EDGE,"E81");Q0=makeQuery(id+"F23.imprint","IMPRINT",FACE,{"disambiguationData":[TD([[makeQuery(id+"F23.imprint","IMPRINT",EDGE,{"derivedFrom":subQ1}),-1.0]])]});}
            var Q1;
            {var subQ1=sQuery(id+"F23.wireOp",EDGE,"E82");Q1=makeQuery(id+"F23.imprint","IMPRINT",FACE,{"disambiguationData":[TD([[makeQuery(id+"F23.imprint","IMPRINT",EDGE,{"derivedFrom":subQ1}),1.0]])]});}
            extrude(context, id + "F24", {"entities" : qUnion([Q0, Q1]), "operationType" : NewBodyOperationType.REMOVE, "oppositeDirection" : true, "depth" : 45 * mm});
        }
        {
            var Q0;
            {var subQ0=sQuery(id+"F19.wireOp",EDGE,"E69");var subQ1=sQuery(id+"F19.wireOp",EDGE,"E75");var subQ2=sQuery(id+"F19.wireOp",EDGE,"E76");Q0=makeQuery(id+"F20.boolean.opBoolean","SPLIT",FACE,{"disambiguationData":[TD([makeQuery(id+"F17.opExtrude","SWEPT_FACE",FACE,{"disambiguationData":[OSD([sQuery(id+"F16.wireOp",EDGE,"E63.0")])]})])],"derivedFrom":makeQuery(id+"F20.opExtrude","CAP_FACE",FACE,{"disambiguationData":[OSD([subQ0,sQuery(id+"F19.wireOp",EDGE,"E70"),subQ1,subQ2])],"isStart":true})});}
            var sketch = newSketch(context, id + "F25", { "sketchPlane" : qUnion([Q0])});
            skPoint(sketch, "E83.0", {"position": v(25.5, -48) * mm});
            skPoint(sketch, "E83.1", {"position": v(25.5, -72) * mm});
            skPoint(sketch, "E83.2", {"position": v(-25.5, -72) * mm});
            skPoint(sketch, "E83.3", {"position": v(-25.5, -48) * mm});
            skSolve(sketch);
        }
        {
            var Q0;
            Q0=makeQuery(id+"F24.boolean.opBoolean","COPY",FACE,{"derivedFrom":makeQuery(id+"F24.opExtrude","SWEPT_FACE",FACE,{"disambiguationData":[OSD([sQuery(id+"F23.wireOp",EDGE,"E81")])]})});
            var sketch = newSketch(context, id + "F26", { "sketchPlane" : qUnion([Q0])});
            skLineSegment(sketch, "E84.bottom", {"start": v(65, -42.74) * mm, "end": v(71, -42.74) * mm});
            skLineSegment(sketch, "E84.top", {"start": v(65, -52.74) * mm, "end": v(71, -52.74) * mm});
            skLineSegment(sketch, "E84.left", {"start": v(65, -42.74) * mm, "end": v(65, -52.74) * mm});
            skLineSegment(sketch, "E84.right", {"start": v(71, -42.74) * mm, "end": v(71, -52.74) * mm});
            skLineSegment(sketch, "E85.bottom", {"start": v(65, -66.74) * mm, "end": v(71, -66.74) * mm});
            skLineSegment(sketch, "E85.top", {"start": v(65, -76.74) * mm, "end": v(71, -76.74) * mm});
            skLineSegment(sketch, "E85.left", {"start": v(65, -66.74) * mm, "end": v(65, -76.74) * mm});
            skLineSegment(sketch, "E85.right", {"start": v(71, -66.74) * mm, "end": v(71, -76.74) * mm});
            skSolve(sketch);
        }
        {
            var Q0;
            Q0=makeQuery(id+"F26.imprint","IMPRINT",FACE,{"disambiguationData":[TD([[makeQuery(id+"F26.imprint","IMPRINT",EDGE,{"derivedFrom":sQuery(id+"F26.wireOp",EDGE,"E84.bottom")}),-1.0]])]});
            var Q1;
            Q1=makeQuery(id+"F26.imprint","IMPRINT",FACE,{"disambiguationData":[TD([[makeQuery(id+"F26.imprint","IMPRINT",EDGE,{"derivedFrom":sQuery(id+"F26.wireOp",EDGE,"E85.bottom")}),-1.0]])]});
            extrude(context, id + "F27", {"entities" : qUnion([Q0, Q1]), "operationType" : NewBodyOperationType.REMOVE, "endBound" : BoundingType.THROUGH_ALL, "oppositeDirection" : true, "depth" : 25 * mm});
        }
        {
            var Q0;
            Q0=makeQuery(id+"F20.boolean.opBoolean","MERGE",FACE,{"derivedFrom":[makeQuery(id+"F17.opExtrude","SWEPT_FACE",FACE,{"disambiguationData":[OSD([sQuery(id+"F16.wireOp",EDGE,"E65")])]}),makeQuery(id+"F20.opExtrude","SWEPT_FACE",FACE,{"disambiguationData":[OSD([sQuery(id+"F19.wireOp",EDGE,"E76")])]})]});
            var sketch = newSketch(context, id + "F28", { "sketchPlane" : qUnion([Q0])});
            skLineSegment(sketch, "E86.0", {"start": v(-21.5, 60) * mm, "end": v(-21.5, 110) * mm});
            skLineSegment(sketch, "E87.0", {"start": v(21.5, 60) * mm, "end": v(21.5, 110) * mm});
            skLineSegment(sketch, "E88", {"start": v(-27.5, 110) * mm, "end": v(-27.5, 60) * mm});
            skLineSegment(sketch, "E89", {"start": v(-27.5, 60) * mm, "end": v(-21.5, 60) * mm});
            skLineSegment(sketch, "E90", {"start": v(-21.5, 110) * mm, "end": v(-27.5, 110) * mm});
            skLineSegment(sketch, "E91", {"start": v(21.5, 110) * mm, "end": v(27.5, 110) * mm});
            skLineSegment(sketch, "E92", {"start": v(27.5, 110) * mm, "end": v(27.5, 60) * mm});
            skLineSegment(sketch, "E93", {"start": v(27.5, 60) * mm, "end": v(21.5, 60) * mm});
            skPoint(sketch, "E94", {"position": v(0, 110) * mm});
            skLineSegment(sketch, "E95", {"start": v(0, 110) * mm, "end": v(0, 50) * mm});
            skCircle(sketch, "E96", {"center": v(0, 85) * mm, "radius": 12.5 * mm});
            skLineSegment(sketch, "E97.rect.bottom", {"start": v(15.5, 100.5) * mm, "end": v(-15.5, 100.5) * mm});
            skLineSegment(sketch, "E97.rect.top", {"start": v(15.5, 69.5) * mm, "end": v(-15.5, 69.5) * mm});
            skLineSegment(sketch, "E97.rect.left", {"start": v(15.5, 100.5) * mm, "end": v(15.5, 69.5) * mm});
            skLineSegment(sketch, "E97.rect.right", {"start": v(-15.5, 100.5) * mm, "end": v(-15.5, 69.5) * mm});
            skSolve(sketch);
        }
        {
            var Q0;
            {var subQ0=sQuery(id+"F28.wireOp",EDGE,"E96");var subQ1=sQuery(id+"F28.wireOp",EDGE,"E95");var subQ3=makeQuery(id+"F28.imprint","INTERSECT",VERTEX,{"disambiguationData":[OD(0.0)],"derivedFrom":[subQ1,subQ0]});Q0=makeQuery(id+"F28.imprint","IMPRINT",FACE,{"disambiguationData":[TD([[makeQuery(id+"F28.imprint","IMPRINT",EDGE,{"disambiguationData":[TD([[subQ3,-1.0]])],"derivedFrom":subQ1}),-1.0]])]});}
            var Q1;
            {var subQ0=sQuery(id+"F28.wireOp",EDGE,"E96");var subQ1=sQuery(id+"F28.wireOp",EDGE,"E95");var subQ3=makeQuery(id+"F28.imprint","INTERSECT",VERTEX,{"disambiguationData":[OD(0.0)],"derivedFrom":[subQ1,subQ0]});Q1=makeQuery(id+"F28.imprint","IMPRINT",FACE,{"disambiguationData":[TD([[makeQuery(id+"F28.imprint","IMPRINT",EDGE,{"disambiguationData":[TD([[subQ3,-1.0]])],"derivedFrom":subQ1}),1.0]])]});}
            extrude(context, id + "F29", {"entities" : qUnion([Q0, Q1]), "operationType" : NewBodyOperationType.REMOVE, "endBound" : BoundingType.UP_TO_NEXT, "oppositeDirection" : true, "depth" : 25 * mm});
        }
        {
            var Q0;
            Q0=sQuery(id+"F25.wireOp",VERTEX,"E83.3");
            var Q1;
            Q1=sQuery(id+"F25.wireOp",VERTEX,"E83.2");
            var Q2;
            Q2=sQuery(id+"F25.wireOp",VERTEX,"E83.0");
            var Q3;
            Q3=sQuery(id+"F25.wireOp",VERTEX,"E83.1");
            var Q4;
            Q4=makeQuery(id+"F17.opExtrude","SWEPT_BODY",BODY,{"disambiguationData":[OSD([sQuery(id+"F16.wireOp",EDGE,"E61.0"),sQuery(id+"F16.wireOp",EDGE,"E62.0"),sQuery(id+"F16.wireOp",EDGE,"E63.0"),sQuery(id+"F16.wireOp",EDGE,"E65")])]});
            hole(context, id + "F30", {"style" : HoleStyle.SIMPLE, "holeDiameter" : 3 * mm, "endStyle" : HoleEndStyle.BLIND, "holeDepth" : 20 * mm, "locations" : qUnion([Q0, Q1, Q2, Q3]), "scope" : qUnion([Q4])});
        }
        {
            var Q0;
            Q0=makeQuery(id+"F20.boolean.opBoolean","MERGE",FACE,{"derivedFrom":[makeQuery(id+"F17.opExtrude","SWEPT_FACE",FACE,{"disambiguationData":[OSD([sQuery(id+"F16.wireOp",EDGE,"E61.0")])]}),makeQuery(id+"F20.opExtrude","SWEPT_FACE",FACE,{"disambiguationData":[OSD([sQuery(id+"F19.wireOp",EDGE,"E75")])]})]});
            var sketch = newSketch(context, id + "F31", { "sketchPlane" : qUnion([Q0])});
            skPoint(sketch, "E98.0", {"position": v(0, -85) * mm});
            skCircle(sketch, "E99", {"center": v(0, -85) * mm, "radius": 6.5 * mm});
            skArc(sketch, "E100", {"start": v(6.8, -93.64) * mm, "mid": v(0, -74) * mm, "end": v(-6.8, -93.64) * mm});
            skCircle(sketch, "E101", {"center": v(0, -85) * mm, "radius": 16 * mm});
            skLineSegment(sketch, "E102", {"start": v(0, -99) * mm, "end": v(6.8, -93.64) * mm});
            skLineSegment(sketch, "E103", {"start": v(0, -99) * mm, "end": v(-6.8, -93.64) * mm});
            skSolve(sketch);
        }
        {
            var Q0;
            Q0=makeQuery(id+"F31.imprint","IMPRINT",FACE,{"disambiguationData":[TD([[makeQuery(id+"F31.imprint","IMPRINT",EDGE,{"derivedFrom":sQuery(id+"F31.wireOp",EDGE,"E99")}),1.0]])]});
            extrude(context, id + "F32", {"entities" : qUnion([Q0]), "operationType" : NewBodyOperationType.REMOVE, "endBound" : BoundingType.UP_TO_NEXT, "oppositeDirection" : true, "depth" : 25 * mm});
        }
        {
            var Q0;
            Q0=makeQuery(id+"F31.imprint","IMPRINT",FACE,{"disambiguationData":[TD([[makeQuery(id+"F31.imprint","IMPRINT",EDGE,{"derivedFrom":sQuery(id+"F31.wireOp",EDGE,"E99")}),-1.0]])]});
            extrude(context, id + "F33", {"entities" : qUnion([Q0]), "operationType" : NewBodyOperationType.REMOVE, "oppositeDirection" : true, "depth" : 5 * mm});
        }
        {
            var Q0;
            Q0=makeQuery(id+"F31.imprint","IMPRINT",FACE,{"disambiguationData":[TD([[makeQuery(id+"F31.imprint","IMPRINT",EDGE,{"derivedFrom":sQuery(id+"F31.wireOp",EDGE,"E100")}),-1.0]])]});
            extrude(context, id + "F34", {"entities" : qUnion([Q0]), "operationType" : NewBodyOperationType.ADD, "depth" : 2 * mm});
        }
        {
            var Q0;
            Q0=makeQuery(id+"F28.imprint","IMPRINT",FACE,{"disambiguationData":[TD([[makeQuery(id+"F28.imprint","IMPRINT",EDGE,{"derivedFrom":sQuery(id+"F28.wireOp",EDGE,"E87.0")}),-1.0]])]});
            var Q1;
            Q1=makeQuery(id+"F28.imprint","IMPRINT",FACE,{"disambiguationData":[TD([[makeQuery(id+"F28.imprint","IMPRINT",EDGE,{"derivedFrom":sQuery(id+"F28.wireOp",EDGE,"E86.0")}),1.0]])]});
            extrude(context, id + "F35", {"entities" : qUnion([Q0, Q1]), "operationType" : NewBodyOperationType.ADD, "depth" : 10 * mm});
        }
        {
            var Q0;
            Q0=makeQuery(id+"F35.opExtrude","CAP_EDGE",EDGE,{"disambiguationData":[OSD([sQuery(id+"F28.wireOp",EDGE,"E90")])],"isStart":false});
            var Q1;
            Q1=makeQuery(id+"F35.opExtrude","CAP_EDGE",EDGE,{"disambiguationData":[OSD([sQuery(id+"F28.wireOp",EDGE,"E91")])],"isStart":false});
            chamfer(context, id + "F36", {"entities" : qUnion([Q0, Q1]), "width" : 5 * mm, "tangentPropagation" : true});
        }
        {
            var Q0;
            Q0=makeQuery(id+"F22.boolean.opBoolean","COPY",FACE,{"derivedFrom":makeQuery(id+"F22.opExtrude","CAP_FACE",FACE,{"disambiguationData":[OSD([sQuery(id+"F21.wireOp",EDGE,"E77.bottom"),sQuery(id+"F21.wireOp",EDGE,"E77.top"),sQuery(id+"F21.wireOp",EDGE,"E77.left"),sQuery(id+"F21.wireOp",EDGE,"E77.right")])],"isStart":false})});
            var sketch = newSketch(context, id + "F37", { "sketchPlane" : qUnion([Q0])});
            skPoint(sketch, "E104", {"position": v(0, -64.79) * mm});
            skLineSegment(sketch, "E105.rect.bottom", {"start": v(18.13, -80.95) * mm, "end": v(-18.13, -80.95) * mm});
            skLineSegment(sketch, "E105.rect.top", {"start": v(18.13, -48.63) * mm, "end": v(-18.13, -48.63) * mm});
            skLineSegment(sketch, "E105.rect.left", {"start": v(18.13, -80.95) * mm, "end": v(18.13, -48.63) * mm});
            skLineSegment(sketch, "E105.rect.right", {"start": v(-18.13, -80.95) * mm, "end": v(-18.13, -48.63) * mm});
            skPoint(sketch, "E106.start.orphan", {"position": v(0, -38.36) * mm});
            skPoint(sketch, "E107.trimOffspring.end.orphan", {"position": v(0, -91.2) * mm});
            skSolve(sketch);
        }
        {
            var Q0;
            Q0=makeQuery(id+"F37.imprint","IMPRINT",FACE,{"disambiguationData":[TD([[makeQuery(id+"F37.imprint","IMPRINT",EDGE,{"derivedFrom":sQuery(id+"F37.wireOp",EDGE,"E105.rect.bottom")}),-1.0]])]});
            extrude(context, id + "F38", {"entities" : qUnion([Q0]), "operationType" : NewBodyOperationType.REMOVE, "oppositeDirection" : true, "depth" : 4 * mm});
        }
        {
            var Q0;
            Q0=makeQuery(id+"F17.opExtrude","CAP_FACE",FACE,{"disambiguationData":[OSD([sQuery(id+"F16.wireOp",EDGE,"E61.0"),sQuery(id+"F16.wireOp",EDGE,"E62.0"),sQuery(id+"F16.wireOp",EDGE,"E63.0"),sQuery(id+"F16.wireOp",EDGE,"E65")])],"isStart":true});
            var sketch = newSketch(context, id + "F39", { "sketchPlane" : qUnion([Q0])});
            skLineSegment(sketch, "E108", {"start": v(0, -91.24) * mm, "end": v(0, -38.24) * mm});
            skPoint(sketch, "E109", {"position": v(0, -74.07) * mm});
            skPoint(sketch, "E110", {"position": v(0, -59.23) * mm});
            skSolve(sketch);
        }
        {
            var Q0;
            Q0=sQuery(id+"F39.wireOp",VERTEX,"E109");
            var Q1;
            Q1=sQuery(id+"F39.wireOp",VERTEX,"E110");
            var Q2;
            Q2=makeQuery(id+"F17.opExtrude","SWEPT_BODY",BODY,{"disambiguationData":[OSD([sQuery(id+"F16.wireOp",EDGE,"E61.0"),sQuery(id+"F16.wireOp",EDGE,"E62.0"),sQuery(id+"F16.wireOp",EDGE,"E63.0"),sQuery(id+"F16.wireOp",EDGE,"E65")])]});
            hole(context, id + "F40", {"style" : HoleStyle.SIMPLE, "holeDiameter" : 5.2 * mm, "endStyle" : HoleEndStyle.THROUGH, "locations" : qUnion([Q0, Q1]), "scope" : qUnion([Q2])});
        }
        {
            var Q0;
            Q0=makeQuery(id+"F27.boolean.opBoolean","SPLIT",FACE,{"disambiguationData":[TD([makeQuery(id+"F27.opExtrude","SWEPT_FACE",FACE,{"disambiguationData":[OSD([sQuery(id+"F26.wireOp",EDGE,"E84.right")])]})])],"derivedFrom":makeQuery(id+"F22.boolean.opBoolean","COPY",FACE,{"derivedFrom":makeQuery(id+"F22.opExtrude","SWEPT_FACE",FACE,{"disambiguationData":[OSD([sQuery(id+"F21.wireOp",EDGE,"E77.bottom")])]})})});
            var sketch = newSketch(context, id + "F41", { "sketchPlane" : qUnion([Q0])});
            skLineSegment(sketch, "E111", {"start": v(0, 65) * mm, "end": v(21.5, 65) * mm});
            skLineSegment(sketch, "E112", {"start": v(-21.5, 65.06) * mm, "end": v(-21.5, 71) * mm});
            skLineSegment(sketch, "E113", {"start": v(-21.5, 71) * mm, "end": v(0, 71) * mm});
            skLineSegment(sketch, "E114", {"start": v(-21.5, 65.06) * mm, "end": v(0, 65) * mm});
            skLineSegment(sketch, "E115", {"start": v(21.47, 65) * mm, "end": v(21.5, 71) * mm});
            skLineSegment(sketch, "E116", {"start": v(21.5, 71) * mm, "end": v(21.5, 65) * mm});
            skLineSegment(sketch, "E117", {"start": v(21.5, 71) * mm, "end": v(0, 71) * mm});
            skSolve(sketch);
        }
        {
            var Q0;
            Q0=makeQuery(id+"F41.imprint","IMPRINT",FACE,{"disambiguationData":[TD([[makeQuery(id+"F41.imprint","IMPRINT",EDGE,{"derivedFrom":sQuery(id+"F41.wireOp",EDGE,"E112")}),-1.0]])]});
            extrude(context, id + "F42", {"entities" : qUnion([Q0]), "operationType" : NewBodyOperationType.ADD, "oppositeDirection" : true, "depth" : 6 * mm});
        }
        {
            var Q0;
            Q0=sQuery(id+"F28.wireOp",VERTEX,"E97.rect.top.start");
            var Q1;
            Q1=sQuery(id+"F28.wireOp",VERTEX,"E97.rect.top.end");
            var Q2;
            Q2=sQuery(id+"F28.wireOp",VERTEX,"E97.rect.right.start");
            var Q3;
            Q3=sQuery(id+"F28.wireOp",VERTEX,"E97.rect.left.start");
            var Q4;
            Q4=makeQuery(id+"F17.opExtrude","SWEPT_BODY",BODY,{"disambiguationData":[OSD([sQuery(id+"F16.wireOp",EDGE,"E61.0"),sQuery(id+"F16.wireOp",EDGE,"E62.0"),sQuery(id+"F16.wireOp",EDGE,"E63.0"),sQuery(id+"F16.wireOp",EDGE,"E65")])]});
            hole(context, id + "F43", {"style" : HoleStyle.SIMPLE, "holeDiameter" : 4 * mm, "endStyle" : HoleEndStyle.THROUGH, "locations" : qUnion([Q0, Q1, Q2, Q3]), "scope" : qUnion([Q4])});
        }
        {
            var Q0;
            Q0=makeQuery(id+"F17.opExtrude","SWEPT_FACE",FACE,{"disambiguationData":[OSD([sQuery(id+"F16.wireOp",EDGE,"E62.0")])]});
            extrude(context, id + "F44", {"entities" : qUnion([Q0]), "operationType" : NewBodyOperationType.ADD, "depth" : 0.4 * mm});
        }
        {
            var Q0;
            Q0=makeQuery(id+"F17.opExtrude","SWEPT_FACE",FACE,{"disambiguationData":[OSD([sQuery(id+"F16.wireOp",EDGE,"E63.0")])]});
            extrude(context, id + "F45", {"entities" : qUnion([Q0]), "operationType" : NewBodyOperationType.ADD, "depth" : 0.4 * mm});
        }
        {
            var Q0;
            {var subQ0=sQuery(id+"F21.wireOp",EDGE,"E77.top");var subQ1=sQuery(id+"F21.wireOp",EDGE,"E77.bottom");var subQ2=makeQuery(id+"F22.opExtrude","CAP_FACE",FACE,{"disambiguationData":[OSD([subQ1,subQ0,sQuery(id+"F21.wireOp",EDGE,"E77.left"),sQuery(id+"F21.wireOp",EDGE,"E77.right")])],"isStart":false});var subQ3=makeQuery(id+"F22.opExtrude","SWEPT_FACE",FACE,{"disambiguationData":[OSD([subQ1])]});var subQ4=sQuery(id+"F19.wireOp",EDGE,"E76");var subQ5=sQuery(id+"F19.wireOp",EDGE,"E75");var subQ6=makeQuery(id+"F20.opExtrude","CAP_FACE",FACE,{"disambiguationData":[OSD([sQuery(id+"F19.wireOp",EDGE,"E69"),sQuery(id+"F19.wireOp",EDGE,"E70"),subQ5,subQ4])],"isStart":true});var subQ7=sQuery(id+"F16.wireOp",EDGE,"E63.0");var subQ8=makeQuery(id+"F17.opExtrude","SWEPT_FACE",FACE,{"disambiguationData":[OSD([subQ7])]});var subQ9=makeQuery(id+"F22.opExtrude","SWEPT_FACE",FACE,{"disambiguationData":[OSD([subQ0])]});var subQ10=makeQuery(id+"F17.opExtrude","CAP_EDGE",EDGE,{"disambiguationData":[OSD([subQ7])],"isStart":false});var subQ11=makeQuery(id+"F20.opExtrude","SWEPT_FACE",FACE,{"disambiguationData":[OSD([subQ4])]});var subQ12=makeQuery(id+"F17.opExtrude","SWEPT_FACE",FACE,{"disambiguationData":[OSD([sQuery(id+"F16.wireOp",EDGE,"E65")])]});var subQ13=makeQuery(id+"F20.opExtrude","SWEPT_FACE",FACE,{"disambiguationData":[OSD([subQ5])]});var subQ14=makeQuery(id+"F17.opExtrude","SWEPT_FACE",FACE,{"disambiguationData":[OSD([sQuery(id+"F16.wireOp",EDGE,"E61.0")])]});var subQ15=sQuery(id+"F16.wireOp",EDGE,"E62.0");var subQ16=makeQuery(id+"F17.opExtrude","SWEPT_FACE",FACE,{"disambiguationData":[OSD([subQ15])]});var subQ17=makeQuery(id+"F17.opExtrude","CAP_EDGE",EDGE,{"disambiguationData":[OSD([subQ15])],"isStart":false});Q0=makeQuery(id+"F45.boolean.opBoolean","MERGE",FACE,{"derivedFrom":[makeQuery(id+"F44.boolean.opBoolean","MERGE",FACE,{"derivedFrom":[makeQuery(id+"F22.boolean.opBoolean","COPY",FACE,{"derivedFrom":subQ2}),makeQuery(id+"F44.opExtrude","SWEPT_FACE",FACE,{"disambiguationData":[OSD([subQ15]),TDD([makeQuery(id+"F22.boolean.opBoolean","SPLIT",EDGE,{"disambiguationData":[TD([subQ14,subQ16,subQ6,subQ13,subQ3,subQ2])],"derivedFrom":subQ17}),makeQuery(id+"F22.boolean.opBoolean","SPLIT",EDGE,{"disambiguationData":[TD([subQ16,subQ12,subQ6,subQ11,subQ2,subQ9])],"derivedFrom":subQ17}),makeQuery(id+"F22.boolean.opBoolean","SPLIT",EDGE,{"disambiguationData":[TD([subQ16,subQ6,subQ3,subQ2,subQ9])],"derivedFrom":subQ17})])]})]}),makeQuery(id+"F45.opExtrude","SWEPT_FACE",FACE,{"disambiguationData":[OSD([subQ7]),TDD([makeQuery(id+"F22.boolean.opBoolean","SPLIT",EDGE,{"disambiguationData":[TD([subQ14,subQ8,subQ6,subQ13,subQ3,subQ2])],"derivedFrom":subQ10}),makeQuery(id+"F22.boolean.opBoolean","SPLIT",EDGE,{"disambiguationData":[TD([subQ8,subQ12,subQ6,subQ11,subQ2,subQ9])],"derivedFrom":subQ10}),makeQuery(id+"F22.boolean.opBoolean","SPLIT",EDGE,{"disambiguationData":[TD([subQ8,subQ6,subQ3,subQ2,subQ9])],"derivedFrom":subQ10})])]})]});}
            extrude(context, id + "F46", {"entities" : qUnion([Q0]), "operationType" : NewBodyOperationType.ADD, "depth" : 2 * mm});
        }
        {
            var Q0;
            Q0=makeQuery(id+"F44.opExtrude","CAP_FACE",FACE,{"disambiguationData":[OSD([sQuery(id+"F16.wireOp",EDGE,"E62.0")])],"isStart":false});
            extrude(context, id + "F47", {"entities" : qUnion([Q0]), "operationType" : NewBodyOperationType.REMOVE, "oppositeDirection" : true, "depth" : 0.5 * mm});
        }
        {
            var Q0;
            Q0=makeQuery(id+"F45.opExtrude","CAP_FACE",FACE,{"disambiguationData":[OSD([sQuery(id+"F16.wireOp",EDGE,"E63.0")])],"isStart":false});
            extrude(context, id + "F48", {"entities" : qUnion([Q0]), "operationType" : NewBodyOperationType.REMOVE, "oppositeDirection" : true, "depth" : 0.5 * mm});
        }
        {
            var Q0;
            Q0=makeQuery(id+"F35.boolean.opBoolean","MERGE",EDGE,{"derivedFrom":[makeQuery(id+"F24.boolean.opBoolean","COPY",EDGE,{"derivedFrom":makeQuery(id+"F24.opExtrude","CAP_EDGE",EDGE,{"disambiguationData":[OSD([sQuery(id+"F23.wireOp",EDGE,"E81")])],"isStart":true})}),makeQuery(id+"F35.opExtrude","SWEPT_EDGE",EDGE,{"disambiguationData":[OSD([sQuery(id+"F28.wireOp",EDGE,"E88"),sQuery(id+"F28.wireOp",EDGE,"E90")])]})]});
            var Q1;
            Q1=makeQuery(id+"F35.boolean.opBoolean","MERGE",EDGE,{"derivedFrom":[makeQuery(id+"F24.boolean.opBoolean","COPY",EDGE,{"derivedFrom":makeQuery(id+"F24.opExtrude","CAP_EDGE",EDGE,{"disambiguationData":[OSD([sQuery(id+"F23.wireOp",EDGE,"E82")])],"isStart":true})}),makeQuery(id+"F35.opExtrude","SWEPT_EDGE",EDGE,{"disambiguationData":[OSD([sQuery(id+"F28.wireOp",EDGE,"E91"),sQuery(id+"F28.wireOp",EDGE,"E92")])]})]});
            var Q2;
            Q2=makeQuery(id+"F20.opExtrude","CAP_EDGE",EDGE,{"disambiguationData":[OSD([sQuery(id+"F19.wireOp",EDGE,"E75")])],"isStart":false});
            var Q3;
            Q3=makeQuery(id+"F24.boolean.opBoolean","COPY",EDGE,{"derivedFrom":makeQuery(id+"F24.opExtrude","SWEPT_EDGE",EDGE,{"disambiguationData":[OSD([sQuery(id+"F19.wireOp",EDGE,"E75"),sQuery(id+"F23.wireOp",EDGE,"E81")])]})});
            var Q4;
            Q4=makeQuery(id+"F24.boolean.opBoolean","COPY",EDGE,{"derivedFrom":makeQuery(id+"F24.opExtrude","SWEPT_EDGE",EDGE,{"disambiguationData":[OSD([sQuery(id+"F19.wireOp",EDGE,"E75"),sQuery(id+"F23.wireOp",EDGE,"E82")])]})});
            var Q5;
            Q5=makeQuery(id+"F36.opChamfer","BLEND_EDGE",EDGE,{"blendedFrom":[makeQuery(id+"F35.opExtrude","CAP_EDGE",EDGE,{"disambiguationData":[OSD([sQuery(id+"F28.wireOp",EDGE,"E90")])],"isStart":false}),makeQuery(id+"F35.boolean.opBoolean","MERGE",FACE,{"derivedFrom":[makeQuery(id+"F24.boolean.opBoolean","COPY",FACE,{"derivedFrom":makeQuery(id+"F24.opExtrude","SWEPT_FACE",FACE,{"disambiguationData":[OSD([sQuery(id+"F23.wireOp",EDGE,"E81")])]})}),makeQuery(id+"F35.opExtrude","SWEPT_FACE",FACE,{"disambiguationData":[OSD([sQuery(id+"F28.wireOp",EDGE,"E88")])]})]})],"blendedInto":[makeQuery(id+"F35.boolean.opBoolean","MERGE",FACE,{"derivedFrom":[makeQuery(id+"F24.boolean.opBoolean","COPY",FACE,{"derivedFrom":makeQuery(id+"F24.opExtrude","SWEPT_FACE",FACE,{"disambiguationData":[OSD([sQuery(id+"F23.wireOp",EDGE,"E81")])]})}),makeQuery(id+"F35.opExtrude","SWEPT_FACE",FACE,{"disambiguationData":[OSD([sQuery(id+"F28.wireOp",EDGE,"E88")])]})]})]});
            var Q6;
            Q6=makeQuery(id+"F35.opExtrude","CAP_EDGE",EDGE,{"disambiguationData":[OSD([sQuery(id+"F28.wireOp",EDGE,"E88")])],"isStart":false});
            var Q7;
            Q7=makeQuery(id+"F36.opChamfer","BLEND_EDGE",EDGE,{"blendedFrom":[makeQuery(id+"F35.opExtrude","CAP_EDGE",EDGE,{"disambiguationData":[OSD([sQuery(id+"F28.wireOp",EDGE,"E91")])],"isStart":false}),makeQuery(id+"F35.boolean.opBoolean","MERGE",FACE,{"derivedFrom":[makeQuery(id+"F24.boolean.opBoolean","COPY",FACE,{"derivedFrom":makeQuery(id+"F24.opExtrude","SWEPT_FACE",FACE,{"disambiguationData":[OSD([sQuery(id+"F23.wireOp",EDGE,"E82")])]})}),makeQuery(id+"F35.opExtrude","SWEPT_FACE",FACE,{"disambiguationData":[OSD([sQuery(id+"F28.wireOp",EDGE,"E92")])]})]})],"blendedInto":[makeQuery(id+"F35.boolean.opBoolean","MERGE",FACE,{"derivedFrom":[makeQuery(id+"F24.boolean.opBoolean","COPY",FACE,{"derivedFrom":makeQuery(id+"F24.opExtrude","SWEPT_FACE",FACE,{"disambiguationData":[OSD([sQuery(id+"F23.wireOp",EDGE,"E82")])]})}),makeQuery(id+"F35.opExtrude","SWEPT_FACE",FACE,{"disambiguationData":[OSD([sQuery(id+"F28.wireOp",EDGE,"E92")])]})]})]});
            var Q8;
            Q8=makeQuery(id+"F35.opExtrude","CAP_EDGE",EDGE,{"disambiguationData":[OSD([sQuery(id+"F28.wireOp",EDGE,"E92")])],"isStart":false});
            var Q9;
            Q9=makeQuery(id+"F22.boolean.opBoolean","COPY",EDGE,{"derivedFrom":makeQuery(id+"F22.opExtrude","CAP_EDGE",EDGE,{"disambiguationData":[OSD([sQuery(id+"F21.wireOp",EDGE,"E77.bottom")])],"isStart":true})});
            var Q10;
            Q10=makeQuery(id+"F22.boolean.opBoolean","COPY",EDGE,{"derivedFrom":makeQuery(id+"F22.opExtrude","CAP_EDGE",EDGE,{"disambiguationData":[OSD([sQuery(id+"F21.wireOp",EDGE,"E77.right")])],"isStart":true})});
            var Q11;
            Q11=makeQuery(id+"F22.boolean.opBoolean","COPY",EDGE,{"derivedFrom":makeQuery(id+"F22.opExtrude","CAP_EDGE",EDGE,{"disambiguationData":[OSD([sQuery(id+"F21.wireOp",EDGE,"E77.top")])],"isStart":true})});
            var Q12;
            Q12=makeQuery(id+"F22.boolean.opBoolean","COPY",EDGE,{"derivedFrom":makeQuery(id+"F22.opExtrude","CAP_EDGE",EDGE,{"disambiguationData":[OSD([sQuery(id+"F21.wireOp",EDGE,"E77.left")])],"isStart":true})});
            var Q13;
            Q13=makeQuery(id+"F46.opExtrude","CAP_EDGE",EDGE,{"disambiguationData":[OSD([sQuery(id+"F37.wireOp",EDGE,"E105.rect.right")])],"isStart":false});
            var Q14;
            Q14=makeQuery(id+"F46.opExtrude","CAP_EDGE",EDGE,{"disambiguationData":[OSD([sQuery(id+"F37.wireOp",EDGE,"E105.rect.top")])],"isStart":false});
            var Q15;
            Q15=makeQuery(id+"F46.opExtrude","CAP_EDGE",EDGE,{"disambiguationData":[OSD([sQuery(id+"F37.wireOp",EDGE,"E105.rect.left")])],"isStart":false});
            var Q16;
            Q16=makeQuery(id+"F46.opExtrude","CAP_EDGE",EDGE,{"disambiguationData":[OSD([sQuery(id+"F37.wireOp",EDGE,"E105.rect.bottom")])],"isStart":false});
            fillet(context, id + "F49", {"entities" : qUnion([Q0, Q1, Q2, Q3, Q4, Q5, Q6, Q7, Q8, Q9, Q10, Q11, Q12, Q13, Q14, Q15, Q16]), "radius" : 2 * mm, "tangentPropagation" : true, "allowEdgeOverflow" : false});
        }
        {
            var Q0;
            Q0=makeQuery(id+"F38.boolean.opBoolean","COPY",EDGE,{"derivedFrom":makeQuery(id+"F38.opExtrude","CAP_EDGE",EDGE,{"disambiguationData":[OSD([sQuery(id+"F37.wireOp",EDGE,"E105.rect.top")])],"isStart":false})});
            var Q1;
            {var subQ0=sQuery(id+"F37.wireOp",EDGE,"E105.rect.right");Q1=makeQuery(id+"F49.opFillet","BLEND_EDGE",EDGE,{"blendedFrom":[makeQuery(id+"F46.opExtrude","CAP_EDGE",EDGE,{"disambiguationData":[OSD([subQ0])],"isStart":false}),makeQuery(id+"F46.boolean.opBoolean","MERGE",FACE,{"derivedFrom":[makeQuery(id+"F38.boolean.opBoolean","COPY",FACE,{"derivedFrom":makeQuery(id+"F38.opExtrude","SWEPT_FACE",FACE,{"disambiguationData":[OSD([subQ0])]})}),makeQuery(id+"F46.opExtrude","SWEPT_FACE",FACE,{"disambiguationData":[OSD([subQ0])]})]})],"blendedInto":[makeQuery(id+"F46.boolean.opBoolean","MERGE",FACE,{"derivedFrom":[makeQuery(id+"F38.boolean.opBoolean","COPY",FACE,{"derivedFrom":makeQuery(id+"F38.opExtrude","SWEPT_FACE",FACE,{"disambiguationData":[OSD([subQ0])]})}),makeQuery(id+"F46.opExtrude","SWEPT_FACE",FACE,{"disambiguationData":[OSD([subQ0])]})]})]});}
            var Q2;
            Q2=makeQuery(id+"F38.boolean.opBoolean","COPY",EDGE,{"derivedFrom":makeQuery(id+"F38.opExtrude","CAP_EDGE",EDGE,{"disambiguationData":[OSD([sQuery(id+"F37.wireOp",EDGE,"E105.rect.bottom")])],"isStart":false})});
            var Q3;
            Q3=makeQuery(id+"F38.boolean.opBoolean","COPY",EDGE,{"derivedFrom":makeQuery(id+"F38.opExtrude","CAP_EDGE",EDGE,{"disambiguationData":[OSD([sQuery(id+"F37.wireOp",EDGE,"E105.rect.left")])],"isStart":false})});
            fillet(context, id + "F50", {"entities" : qUnion([Q0, Q1, Q2, Q3]), "radius" : 3 * mm, "tangentPropagation" : true, "allowEdgeOverflow" : false});
        }
        {
            var Q0;
            Q0=makeQuery(id+"F34.opExtrude","CAP_EDGE",EDGE,{"disambiguationData":[OSD([sQuery(id+"F31.wireOp",EDGE,"E101")])],"isStart":false});
            fillet(context, id + "F51", {"entities" : qUnion([Q0]), "radius" : 2 * mm, "tangentPropagation" : true, "allowEdgeOverflow" : false});
        }
        {
            var Q0;
            Q0=makeQuery(id+"F27.boolean.opBoolean","INTERSECT",EDGE,{"derivedFrom":[makeQuery(id+"F27.opExtrude","SWEPT_FACE",FACE,{"disambiguationData":[OSD([sQuery(id+"F26.wireOp",EDGE,"E84.left")])]}),makeQuery(id+"F27.opExtrude","SWEPT_FACE",FACE,{"disambiguationData":[OSD([sQuery(id+"F26.wireOp",EDGE,"E85.left")])]})]});
            var Q1;
            Q1=makeQuery(id+"F24.boolean.opBoolean","COPY",EDGE,{"derivedFrom":makeQuery(id+"F24.opExtrude","CAP_EDGE",EDGE,{"disambiguationData":[OSD([sQuery(id+"F19.wireOp",EDGE,"E69")])],"isStart":false})});
            fillet(context, id + "F52", {"entities" : qUnion([Q0, Q1]), "radius" : 3 * mm, "tangentPropagation" : true, "allowEdgeOverflow" : false});
        }
    });
